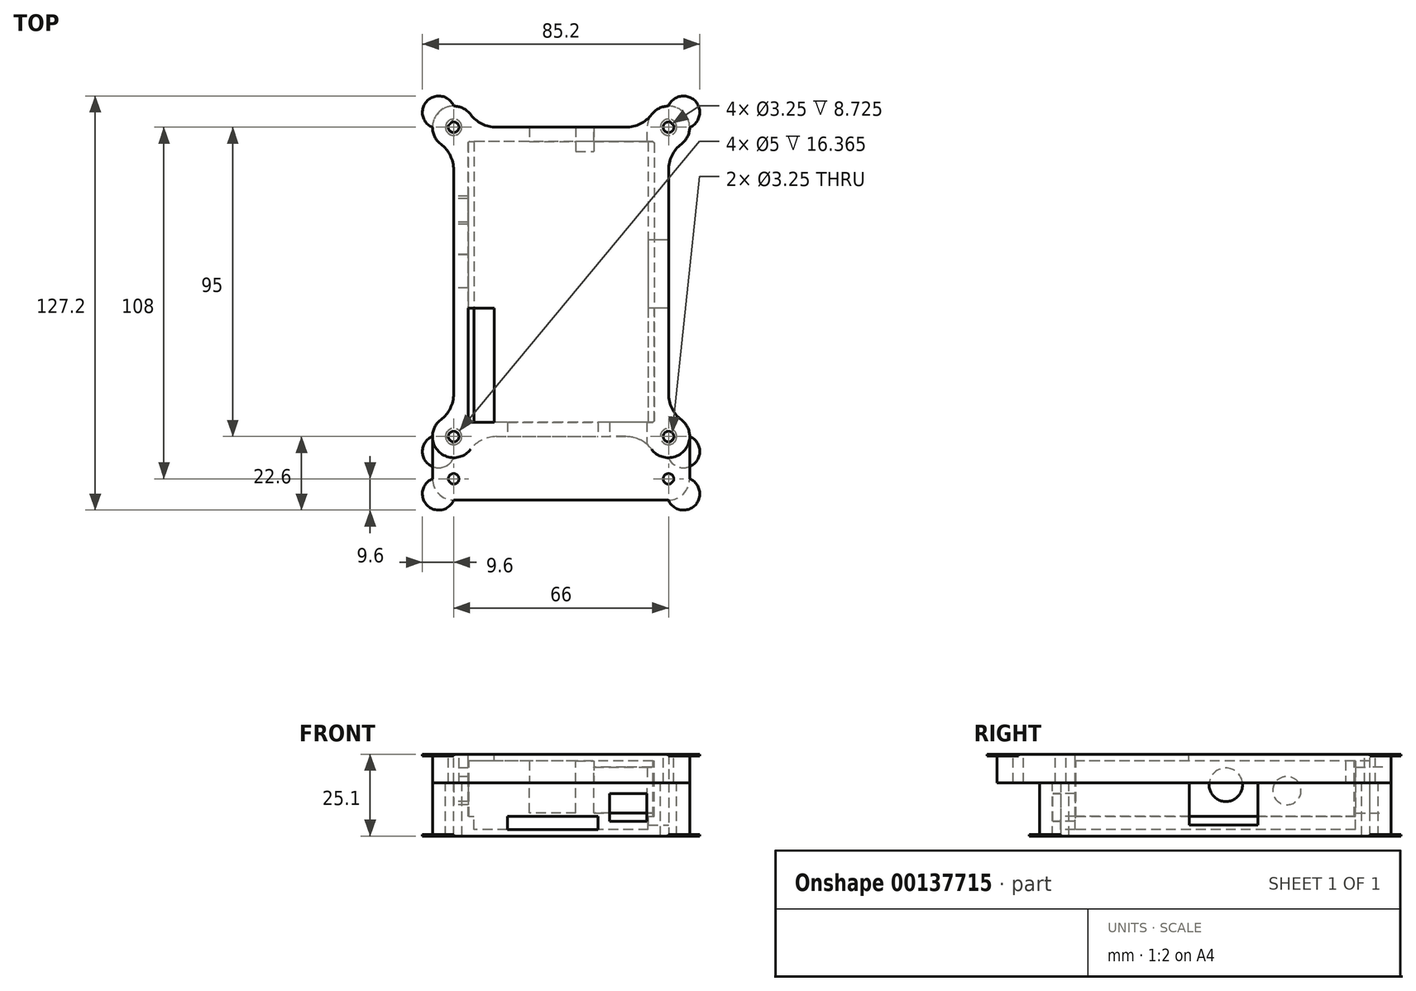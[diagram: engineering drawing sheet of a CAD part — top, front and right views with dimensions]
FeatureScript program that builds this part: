
annotation { "Feature Type Name" : "Feature", "Feature Type Description" : "" }
export const myFeature = defineFeature(function(context is Context, id is Id, definition is map)
    precondition{}
    {
        {
            var Q0;
            Q0=qCreatedBy(makeId("Top.planeOp"),FACE);
            var sketch = newSketch(context, id + "F0", { "sketchPlane" : qUnion([Q0])});
            skLineSegment(sketch, "E0.rect.bottom", {"start": v(28, 42.5) * mm, "end": v(-28, 42.5) * mm, "construction": true});
            skLineSegment(sketch, "E0.rect.top", {"start": v(28, -42.5) * mm, "end": v(-28, -42.5) * mm, "construction": true});
            skLineSegment(sketch, "E0.rect.left", {"start": v(28, 42.5) * mm, "end": v(28, -42.5) * mm, "construction": true});
            skLineSegment(sketch, "E0.rect.right", {"start": v(-28, 42.5) * mm, "end": v(-28, -42.5) * mm, "construction": true});
            skPoint(sketch, "E0.rect.middle", {"position": v(0, 0) * mm});
            skLineSegment(sketch, "E1.0", {"start": v(33, 47.5) * mm, "end": v(-33, 47.5) * mm});
            skLineSegment(sketch, "E1.1", {"start": v(33, 47.5) * mm, "end": v(33, -47.5) * mm});
            skLineSegment(sketch, "E1.2", {"start": v(33, -47.5) * mm, "end": v(-33, -47.5) * mm});
            skLineSegment(sketch, "E1.3", {"start": v(-33, 47.5) * mm, "end": v(-33, -47.5) * mm});
            skSolve(sketch);
        }
        {
            var Q0;
            Q0=qSketchRegion(id+"F0",true);
            extrude(context, id + "F1", {"entities" : qUnion([Q0]), "depth" : (2 + 1.6 + 15.5 + 4) * mm});
        }
        {
            var Q0;
            Q0=makeQuery(id+"F1.opExtrude","CAP_FACE",FACE,{"disambiguationData":[OSD([sQuery(id+"F0.wireOp",EDGE,"E1.0"),sQuery(id+"F0.wireOp",EDGE,"E1.1"),sQuery(id+"F0.wireOp",EDGE,"E1.2"),sQuery(id+"F0.wireOp",EDGE,"E1.3")])],"isStart":false});
            var sketch = newSketch(context, id + "F2", { "sketchPlane" : qUnion([Q0])});
            skLineSegment(sketch, "E2.rect.bottom", {"start": v(28, 42.5) * mm, "end": v(-28, 42.5) * mm});
            skLineSegment(sketch, "E2.rect.top", {"start": v(28, -42.5) * mm, "end": v(-28, -42.5) * mm});
            skLineSegment(sketch, "E2.rect.left", {"start": v(28, 42.5) * mm, "end": v(28, -42.5) * mm});
            skLineSegment(sketch, "E2.rect.right", {"start": v(-28, 42.5) * mm, "end": v(-28, -42.5) * mm});
            skPoint(sketch, "E2.rect.middle", {"position": v(0, 0) * mm});
            skSolve(sketch);
        }
        {
            var Q0;
            Q0=qSketchRegion(id+"F2",true);
            extrude(context, id + "F3", {"entities" : qUnion([Q0]), "operationType" : NewBodyOperationType.REMOVE, "oppositeDirection" : true, "depth" : (15.5 + 1.6) * mm});
        }
        {
            var Q0;
            Q0=makeQuery(id+"F3.boolean.opBoolean","COPY",FACE,{"derivedFrom":makeQuery(id+"F3.opExtrude","CAP_FACE",FACE,{"disambiguationData":[OSD([sQuery(id+"F2.wireOp",EDGE,"E2.rect.bottom"),sQuery(id+"F2.wireOp",EDGE,"E2.rect.top"),sQuery(id+"F2.wireOp",EDGE,"E2.rect.left"),sQuery(id+"F2.wireOp",EDGE,"E2.rect.right")])],"isStart":false})});
            var sketch = newSketch(context, id + "F4", { "sketchPlane" : qUnion([Q0])});
            skLineSegment(sketch, "E3.rect.bottom", {"start": v(26.75, 42.5) * mm, "end": v(-26.75, 42.5) * mm});
            skLineSegment(sketch, "E3.rect.top", {"start": v(26.75, -42.5) * mm, "end": v(-26.75, -42.5) * mm});
            skLineSegment(sketch, "E3.rect.left", {"start": v(26.75, 42.5) * mm, "end": v(26.75, -42.5) * mm});
            skLineSegment(sketch, "E3.rect.right", {"start": v(-26.75, 42.5) * mm, "end": v(-26.75, -42.5) * mm});
            skPoint(sketch, "E3.rect.middle", {"position": v(0, 0) * mm});
            skSolve(sketch);
        }
        {
            var Q0;
            Q0=qSketchRegion(id+"F4",true);
            extrude(context, id + "F5", {"entities" : qUnion([Q0]), "operationType" : NewBodyOperationType.REMOVE, "oppositeDirection" : true, "depth" : 4 * mm});
        }
        {
            var Q0;
            Q0=makeQuery(id+"F1.opExtrude","SWEPT_FACE",FACE,{"disambiguationData":[OSD([sQuery(id+"F0.wireOp",EDGE,"E1.2")])]});
            var sketch = newSketch(context, id + "F6", { "sketchPlane" : qUnion([Q0])});
            skLineSegment(sketch, "E4.0", {"start": v(26.75, 2) * mm, "end": v(-26.75, 2) * mm, "construction": true});
            skLineSegment(sketch, "E4.1", {"start": v(-26.75, 6) * mm, "end": v(-28, 6) * mm, "construction": true});
            skLineSegment(sketch, "E5.bottom", {"start": v(-16.5, 2) * mm, "end": v(11.3, 2) * mm});
            skLineSegment(sketch, "E5.top", {"start": v(-16.5, 6) * mm, "end": v(11.3, 6) * mm});
            skLineSegment(sketch, "E5.left", {"start": v(-16.5, 2) * mm, "end": v(-16.5, 6) * mm});
            skLineSegment(sketch, "E5.right", {"start": v(11.3, 2) * mm, "end": v(11.3, 6) * mm});
            skLineSegment(sketch, "E6.0", {"start": v(28, 6) * mm, "end": v(26.75, 6) * mm, "construction": true});
            skLineSegment(sketch, "E7.bottom", {"start": v(24.4, 7.6) * mm, "end": v(16.8, 7.6) * mm, "construction": true});
            skLineSegment(sketch, "E7.top", {"start": v(24.4, 10) * mm, "end": v(16.8, 10) * mm, "construction": true});
            skLineSegment(sketch, "E7.left", {"start": v(24.4, 7.6) * mm, "end": v(24.4, 10) * mm, "construction": true});
            skLineSegment(sketch, "E7.right", {"start": v(16.8, 7.6) * mm, "end": v(16.8, 10) * mm, "construction": true});
            skLineSegment(sketch, "E8", {"start": v(20.6, 10) * mm, "end": v(20.6, 7.6) * mm, "construction": true});
            skPoint(sketch, "E9", {"position": v(20.6, 8.8) * mm});
            skLineSegment(sketch, "E10.rect.bottom", {"start": v(26.35, 13.05) * mm, "end": v(14.85, 13.05) * mm});
            skLineSegment(sketch, "E10.rect.top", {"start": v(26.35, 4.55) * mm, "end": v(14.85, 4.55) * mm});
            skLineSegment(sketch, "E10.rect.left", {"start": v(26.35, 13.05) * mm, "end": v(26.35, 4.55) * mm});
            skLineSegment(sketch, "E10.rect.right", {"start": v(14.85, 13.05) * mm, "end": v(14.85, 4.55) * mm});
            skSolve(sketch);
        }
        {
            var Q0;
            Q0=qSketchRegion(id+"F6",true);
            var Q1;
            Q1=makeQuery(id+"F5.boolean.opBoolean","MERGE",FACE,{"derivedFrom":[makeQuery(id+"F3.boolean.opBoolean","COPY",FACE,{"derivedFrom":makeQuery(id+"F3.opExtrude","SWEPT_FACE",FACE,{"disambiguationData":[OSD([sQuery(id+"F2.wireOp",EDGE,"E2.rect.top")])]})}),makeQuery(id+"F5.opExtrude","SWEPT_FACE",FACE,{"disambiguationData":[OSD([sQuery(id+"F4.wireOp",EDGE,"E3.rect.top")])]})]});
            extrude(context, id + "F7", {"entities" : qUnion([Q0]), "operationType" : NewBodyOperationType.REMOVE, "endBound" : BoundingType.UP_TO_SURFACE, "oppositeDirection" : true, "endBoundEntityFace" : qUnion([Q1]), "depth" : 25 * mm});
        }
        {
            var Q0;
            Q0=makeQuery(id+"F1.opExtrude","SWEPT_FACE",FACE,{"disambiguationData":[OSD([sQuery(id+"F0.wireOp",EDGE,"E1.0")])]});
            var sketch = newSketch(context, id + "F8", { "sketchPlane" : qUnion([Q0])});
            skLineSegment(sketch, "E11.0", {"start": v(-28, 6) * mm, "end": v(-26.75, 6) * mm, "construction": true});
            skLineSegment(sketch, "E11.1", {"start": v(-26.75, 2) * mm, "end": v(26.75, 2) * mm, "construction": true});
            skLineSegment(sketch, "E11.2", {"start": v(26.75, 6) * mm, "end": v(28, 6) * mm, "construction": true});
            skLineSegment(sketch, "E12.bottom", {"start": v(-26, 7.6) * mm, "end": v(-10.6, 7.6) * mm, "construction": true});
            skLineSegment(sketch, "E12.top", {"start": v(-26, 20.6) * mm, "end": v(-10.6, 20.6) * mm, "construction": true});
            skLineSegment(sketch, "E12.left", {"start": v(-26, 7.6) * mm, "end": v(-26, 20.6) * mm, "construction": true});
            skLineSegment(sketch, "E12.right", {"start": v(-10.6, 7.6) * mm, "end": v(-10.6, 20.6) * mm, "construction": true});
            skLineSegment(sketch, "E13.bottom", {"start": v(-4.05, 7.6) * mm, "end": v(9.2, 7.6) * mm, "construction": true});
            skLineSegment(sketch, "E13.top", {"start": v(-4.05, 23.1) * mm, "end": v(9.2, 23.1) * mm, "construction": true});
            skLineSegment(sketch, "E13.left", {"start": v(-4.05, 7.6) * mm, "end": v(-4.05, 23.1) * mm, "construction": true});
            skLineSegment(sketch, "E13.right", {"start": v(9.2, 7.6) * mm, "end": v(9.2, 23.1) * mm, "construction": true});
            skLineSegment(sketch, "E14.0", {"start": v(-26.5, 21.1) * mm, "end": v(-10.1, 21.1) * mm});
            skLineSegment(sketch, "E14.1", {"start": v(-26.5, 7.1) * mm, "end": v(-26.5, 21.1) * mm});
            skLineSegment(sketch, "E14.2", {"start": v(-26.5, 7.1) * mm, "end": v(-10.1, 7.1) * mm});
            skLineSegment(sketch, "E14.3", {"start": v(-10.1, 7.1) * mm, "end": v(-10.1, 21.1) * mm});
            skLineSegment(sketch, "E15.0", {"start": v(-4.55, 23.6) * mm, "end": v(9.7, 23.6) * mm});
            skLineSegment(sketch, "E15.1", {"start": v(-4.55, 7.1) * mm, "end": v(-4.55, 23.6) * mm});
            skLineSegment(sketch, "E15.2", {"start": v(-4.55, 7.1) * mm, "end": v(9.7, 7.1) * mm});
            skLineSegment(sketch, "E15.3", {"start": v(9.7, 7.1) * mm, "end": v(9.7, 23.6) * mm});
            skSolve(sketch);
        }
        {
            var Q0;
            Q0=qSketchRegion(id+"F8",true);
            var Q1;
            Q1=makeQuery(id+"F5.boolean.opBoolean","MERGE",FACE,{"derivedFrom":[makeQuery(id+"F3.boolean.opBoolean","COPY",FACE,{"derivedFrom":makeQuery(id+"F3.opExtrude","SWEPT_FACE",FACE,{"disambiguationData":[OSD([sQuery(id+"F2.wireOp",EDGE,"E2.rect.bottom")])]})}),makeQuery(id+"F5.opExtrude","SWEPT_FACE",FACE,{"disambiguationData":[OSD([sQuery(id+"F4.wireOp",EDGE,"E3.rect.bottom")])]})]});
            extrude(context, id + "F9", {"entities" : qUnion([Q0]), "operationType" : NewBodyOperationType.REMOVE, "endBound" : BoundingType.UP_TO_SURFACE, "oppositeDirection" : true, "endBoundEntityFace" : qUnion([Q1]), "depth" : 25 * mm});
        }
        {
            var Q0;
            Q0=makeQuery(id+"F1.opExtrude","SWEPT_FACE",FACE,{"disambiguationData":[OSD([sQuery(id+"F0.wireOp",EDGE,"E1.1")])]});
            var sketch = newSketch(context, id + "F10", { "sketchPlane" : qUnion([Q0])});
            skLineSegment(sketch, "E16.0", {"start": v(42.5, 6) * mm, "end": v(-42.5, 6) * mm, "construction": true});
            skLineSegment(sketch, "E17.bottom", {"start": v(-5, 6.8) * mm, "end": v(10.1, 6.8) * mm, "construction": true});
            skLineSegment(sketch, "E17.top", {"start": v(-5, 12.95) * mm, "end": v(10.1, 12.95) * mm, "construction": true});
            skLineSegment(sketch, "E17.left", {"start": v(-5, 6.8) * mm, "end": v(-5, 12.95) * mm, "construction": true});
            skLineSegment(sketch, "E17.right", {"start": v(10.1, 6.8) * mm, "end": v(10.1, 12.95) * mm, "construction": true});
            skLineSegment(sketch, "E18", {"start": v(2.55, 12.95) * mm, "end": v(2.55, 6.8) * mm, "construction": true});
            skPoint(sketch, "E19", {"position": v(2.55, 9.88) * mm});
            skLineSegment(sketch, "E20.rect.bottom", {"start": v(13.05, 16.38) * mm, "end": v(-7.95, 16.38) * mm});
            skLineSegment(sketch, "E20.rect.top", {"start": v(13.05, 3.38) * mm, "end": v(-7.95, 3.38) * mm});
            skLineSegment(sketch, "E20.rect.left", {"start": v(13.05, 16.38) * mm, "end": v(13.05, 3.38) * mm});
            skLineSegment(sketch, "E20.rect.right", {"start": v(-7.95, 16.38) * mm, "end": v(-7.95, 3.38) * mm});
            skSolve(sketch);
        }
        {
            var Q0;
            Q0=qSketchRegion(id+"F10",true);
            var Q1;
            Q1=makeQuery(id+"F5.boolean.opBoolean","COPY",FACE,{"derivedFrom":makeQuery(id+"F5.opExtrude","SWEPT_FACE",FACE,{"disambiguationData":[OSD([sQuery(id+"F4.wireOp",EDGE,"E3.rect.left")])]})});
            extrude(context, id + "F11", {"entities" : qUnion([Q0]), "operationType" : NewBodyOperationType.REMOVE, "endBound" : BoundingType.UP_TO_SURFACE, "oppositeDirection" : true, "endBoundEntityFace" : qUnion([Q1]), "depth" : 25 * mm});
        }
        {
            var Q0;
            Q0=makeQuery(id+"F1.opExtrude","SWEPT_FACE",FACE,{"disambiguationData":[OSD([sQuery(id+"F0.wireOp",EDGE,"E1.3")])]});
            var sketch = newSketch(context, id + "F12", { "sketchPlane" : qUnion([Q0])});
            skLineSegment(sketch, "E21.0", {"start": v(-42.5, 6) * mm, "end": v(42.5, 6) * mm, "construction": true});
            skCircle(sketch, "E22", {"center": v(-22, 13.95) * mm, "radius": 3.35 * mm, "construction": true});
            skCircle(sketch, "E23", {"center": v(-3.25, 15.75) * mm, "radius": 4.15 * mm, "construction": true});
            skPoint(sketch, "E24", {"position": v(-22, 10.6) * mm});
            skPoint(sketch, "E25", {"position": v(-3.25, 11.6) * mm});
            skCircle(sketch, "E26.0", {"center": v(-22, 13.95) * mm, "radius": 4.35 * mm});
            skCircle(sketch, "E27.0", {"center": v(-3.25, 15.75) * mm, "radius": 5.15 * mm});
            skSolve(sketch);
        }
        {
            var Q0;
            Q0=qSketchRegion(id+"F12",true);
            var Q1;
            Q1=makeQuery(id+"F3.boolean.opBoolean","COPY",FACE,{"derivedFrom":makeQuery(id+"F3.opExtrude","SWEPT_FACE",FACE,{"disambiguationData":[OSD([sQuery(id+"F2.wireOp",EDGE,"E2.rect.right")])]})});
            extrude(context, id + "F13", {"entities" : qUnion([Q0]), "operationType" : NewBodyOperationType.REMOVE, "endBound" : BoundingType.UP_TO_SURFACE, "oppositeDirection" : true, "endBoundEntityFace" : qUnion([Q1]), "depth" : 25 * mm});
        }
        {
            var Q0;
            Q0=makeQuery(id+"F1.opExtrude","CAP_FACE",FACE,{"disambiguationData":[OSD([sQuery(id+"F0.wireOp",EDGE,"E1.0"),sQuery(id+"F0.wireOp",EDGE,"E1.1"),sQuery(id+"F0.wireOp",EDGE,"E1.2"),sQuery(id+"F0.wireOp",EDGE,"E1.3")])],"isStart":false});
            var sketch = newSketch(context, id + "F14", { "sketchPlane" : qUnion([Q0])});
            skLineSegment(sketch, "E28.rect.bottom", {"start": v(28.58, 43.08) * mm, "end": v(-28.57, 43.08) * mm});
            skLineSegment(sketch, "E28.rect.top", {"start": v(28.57, -43.07) * mm, "end": v(-28.58, -43.07) * mm});
            skLineSegment(sketch, "E28.rect.left", {"start": v(28.58, 43.08) * mm, "end": v(28.57, -43.07) * mm});
            skLineSegment(sketch, "E28.rect.right", {"start": v(-28.57, 43.08) * mm, "end": v(-28.58, -43.07) * mm});
            skPoint(sketch, "E28.rect.middle", {"position": v(0, 0) * mm});
            skSolve(sketch);
        }
        {
            var Q0;
            Q0=qSketchRegion(id+"F14",true);
            var Q1;
            {var subQ0=sQuery(id+"F2.wireOp",EDGE,"E2.rect.bottom");var subQ1=sQuery(id+"F2.wireOp",EDGE,"E2.rect.top");var subQ2=sQuery(id+"F2.wireOp",EDGE,"E2.rect.right");Q1=makeQuery(id+"F5.boolean.opBoolean","SPLIT",FACE,{"disambiguationData":[TD([makeQuery(id+"F3.boolean.opBoolean","COPY",FACE,{"derivedFrom":makeQuery(id+"F3.opExtrude","SWEPT_FACE",FACE,{"disambiguationData":[OSD([subQ2])]})})])],"derivedFrom":makeQuery(id+"F3.boolean.opBoolean","COPY",FACE,{"derivedFrom":makeQuery(id+"F3.opExtrude","CAP_FACE",FACE,{"disambiguationData":[OSD([subQ0,subQ1,sQuery(id+"F2.wireOp",EDGE,"E2.rect.left"),subQ2])],"isStart":false})})});}
            extrude(context, id + "F15", {"entities" : qUnion([Q0]), "operationType" : NewBodyOperationType.REMOVE, "endBound" : BoundingType.UP_TO_SURFACE, "oppositeDirection" : true, "endBoundEntityFace" : qUnion([Q1]), "depth" : 25 * mm});
        }
        {
            var Q0;
            {var subQ2=sQuery(id+"F2.wireOp",EDGE,"E2.rect.left");var subQ3=makeQuery(id+"F3.boolean.opBoolean","COPY",FACE,{"derivedFrom":makeQuery(id+"F3.opExtrude","SWEPT_FACE",FACE,{"disambiguationData":[OSD([subQ2])]})});var subQ4=sQuery(id+"F2.wireOp",EDGE,"E2.rect.bottom");var subQ5=makeQuery(id+"F3.boolean.opBoolean","COPY",FACE,{"derivedFrom":makeQuery(id+"F3.opExtrude","SWEPT_FACE",FACE,{"disambiguationData":[OSD([subQ4])]})});var subQ6=sQuery(id+"F2.wireOp",EDGE,"E2.rect.top");var subQ9=sQuery(id+"F2.wireOp",EDGE,"E2.rect.right");var subQ10=makeQuery(id+"F3.boolean.opBoolean","COPY",FACE,{"derivedFrom":makeQuery(id+"F3.opExtrude","CAP_FACE",FACE,{"disambiguationData":[OSD([subQ4,subQ6,subQ2,subQ9])],"isStart":false})});Q0=makeQuery(id+"F15.boolean.opBoolean","MERGE",FACE,{"derivedFrom":[makeQuery(id+"F5.boolean.opBoolean","SPLIT",FACE,{"disambiguationData":[TD([makeQuery(id+"F3.boolean.opBoolean","COPY",FACE,{"derivedFrom":makeQuery(id+"F3.opExtrude","SWEPT_FACE",FACE,{"disambiguationData":[OSD([subQ9])]})})])],"derivedFrom":subQ10}),makeQuery(id+"F11.boolean.opBoolean","SPLIT",FACE,{"disambiguationData":[TD([subQ5])],"derivedFrom":makeQuery(id+"F5.boolean.opBoolean","SPLIT",FACE,{"disambiguationData":[TD([subQ3])],"derivedFrom":subQ10})}),makeQuery(id+"F15.opExtrude","CAP_FACE",FACE,{"disambiguationData":[OSD([sQuery(id+"F14.wireOp",EDGE,"E28.rect.bottom"),sQuery(id+"F14.wireOp",EDGE,"E28.rect.top"),sQuery(id+"F14.wireOp",EDGE,"E28.rect.left"),sQuery(id+"F14.wireOp",EDGE,"E28.rect.right")])],"isStart":false})]});}
            var sketch = newSketch(context, id + "F16", { "sketchPlane" : qUnion([Q0])});
            skLineSegment(sketch, "E29.bottom", {"start": v(-26.75, 42.5) * mm, "end": v(26.75, 42.5) * mm});
            skLineSegment(sketch, "E29.top", {"start": v(-26.75, 43.08) * mm, "end": v(26.75, 43.08) * mm});
            skLineSegment(sketch, "E29.left", {"start": v(-26.75, 42.5) * mm, "end": v(-26.75, 43.08) * mm});
            skLineSegment(sketch, "E29.right", {"start": v(26.75, 42.5) * mm, "end": v(26.75, 43.08) * mm});
            skLineSegment(sketch, "E30.bottom", {"start": v(-26.75, -42.5) * mm, "end": v(26.75, -42.5) * mm});
            skLineSegment(sketch, "E30.top", {"start": v(-26.75, -43.07) * mm, "end": v(26.75, -43.07) * mm});
            skLineSegment(sketch, "E30.left", {"start": v(-26.75, -42.5) * mm, "end": v(-26.75, -43.07) * mm});
            skLineSegment(sketch, "E30.right", {"start": v(26.75, -42.5) * mm, "end": v(26.75, -43.07) * mm});
            skSolve(sketch);
        }
        {
            var Q0;
            Q0=qSketchRegion(id+"F16",true);
            var Q1;
            Q1=makeQuery(id+"F7.boolean.opBoolean","MERGE",FACE,{"derivedFrom":[makeQuery(id+"F5.boolean.opBoolean","COPY",FACE,{"derivedFrom":makeQuery(id+"F5.opExtrude","CAP_FACE",FACE,{"disambiguationData":[OSD([sQuery(id+"F4.wireOp",EDGE,"E3.rect.bottom"),sQuery(id+"F4.wireOp",EDGE,"E3.rect.top"),sQuery(id+"F4.wireOp",EDGE,"E3.rect.left"),sQuery(id+"F4.wireOp",EDGE,"E3.rect.right")])],"isStart":false})}),makeQuery(id+"F7.opExtrude","SWEPT_FACE",FACE,{"disambiguationData":[OSD([sQuery(id+"F6.wireOp",EDGE,"E5.bottom")])]})]});
            extrude(context, id + "F17", {"entities" : qUnion([Q0]), "operationType" : NewBodyOperationType.REMOVE, "endBound" : BoundingType.UP_TO_SURFACE, "oppositeDirection" : true, "endBoundEntityFace" : qUnion([Q1]), "depth" : 25 * mm});
        }
        {
            var Q0;
            Q0=makeQuery(id+"F1.opExtrude","CAP_FACE",FACE,{"disambiguationData":[OSD([sQuery(id+"F0.wireOp",EDGE,"E1.0"),sQuery(id+"F0.wireOp",EDGE,"E1.1"),sQuery(id+"F0.wireOp",EDGE,"E1.2"),sQuery(id+"F0.wireOp",EDGE,"E1.3")])],"isStart":false});
            var sketch = newSketch(context, id + "F18", { "sketchPlane" : qUnion([Q0])});
            skLineSegment(sketch, "E31.bottom", {"start": v(-33, 47.5) * mm, "end": v(33, 47.5) * mm});
            skLineSegment(sketch, "E31.top", {"start": v(-33, -47.5) * mm, "end": v(33, -47.5) * mm});
            skLineSegment(sketch, "E31.left", {"start": v(-33, 47.5) * mm, "end": v(-33, -47.5) * mm});
            skLineSegment(sketch, "E31.right", {"start": v(33, 47.5) * mm, "end": v(33, -47.5) * mm});
            skSolve(sketch);
        }
        {
            var Q0;
            Q0=qSketchRegion(id+"F18",true);
            extrude(context, id + "F19", {"entities" : qUnion([Q0]), "operationType" : NewBodyOperationType.ADD, "depth" : 2 * mm});
        }
        {
            var Q0;
            Q0=makeQuery(id+"F19.opExtrude","CAP_FACE",FACE,{"disambiguationData":[OSD([sQuery(id+"F18.wireOp",EDGE,"E31.bottom"),sQuery(id+"F18.wireOp",EDGE,"E31.top"),sQuery(id+"F18.wireOp",EDGE,"E31.left"),sQuery(id+"F18.wireOp",EDGE,"E31.right")])],"isStart":false});
            var sketch = newSketch(context, id + "F20", { "sketchPlane" : qUnion([Q0])});
            skCircle(sketch, "E32", {"center": v(-33, 47.5) * mm, "radius": 6.5 * mm});
            skCircle(sketch, "E33", {"center": v(33, 47.5) * mm, "radius": 6.5 * mm});
            skCircle(sketch, "E34", {"center": v(33, -47.5) * mm, "radius": 6.5 * mm});
            skCircle(sketch, "E35", {"center": v(-33, -47.5) * mm, "radius": 6.5 * mm});
            skSolve(sketch);
        }
        {
            var Q0;
            Q0=qSketchRegion(id+"F20",true);
            var Q1;
            Q1=makeQuery(id+"F1.opExtrude","CAP_FACE",FACE,{"disambiguationData":[OSD([sQuery(id+"F0.wireOp",EDGE,"E1.0"),sQuery(id+"F0.wireOp",EDGE,"E1.1"),sQuery(id+"F0.wireOp",EDGE,"E1.2"),sQuery(id+"F0.wireOp",EDGE,"E1.3")])],"isStart":true});
            extrude(context, id + "F21", {"entities" : qUnion([Q0]), "operationType" : NewBodyOperationType.ADD, "endBound" : BoundingType.UP_TO_SURFACE, "oppositeDirection" : true, "endBoundEntityFace" : qUnion([Q1]), "depth" : 25 * mm});
        }
        {
            var Q0;
            Q0=makeQuery(id+"F21.boolean.opBoolean","MERGE",FACE,{"derivedFrom":[makeQuery(id+"F19.opExtrude","CAP_FACE",FACE,{"disambiguationData":[OSD([sQuery(id+"F18.wireOp",EDGE,"E31.bottom"),sQuery(id+"F18.wireOp",EDGE,"E31.top"),sQuery(id+"F18.wireOp",EDGE,"E31.left"),sQuery(id+"F18.wireOp",EDGE,"E31.right")])],"isStart":false}),makeQuery(id+"F21.opExtrude","CAP_FACE",FACE,{"disambiguationData":[OSD([sQuery(id+"F20.wireOp",EDGE,"E32")])],"isStart":true}),makeQuery(id+"F21.opExtrude","CAP_FACE",FACE,{"disambiguationData":[OSD([sQuery(id+"F20.wireOp",EDGE,"E33")])],"isStart":true}),makeQuery(id+"F21.opExtrude","CAP_FACE",FACE,{"disambiguationData":[OSD([sQuery(id+"F20.wireOp",EDGE,"E34")])],"isStart":true}),makeQuery(id+"F21.opExtrude","CAP_FACE",FACE,{"disambiguationData":[OSD([sQuery(id+"F20.wireOp",EDGE,"E35")])],"isStart":true})]});
            var sketch = newSketch(context, id + "F22", { "sketchPlane" : qUnion([Q0])});
            skCircle(sketch, "E36", {"center": v(-33, -47.5) * mm, "radius": 1.63 * mm});
            skCircle(sketch, "E37", {"center": v(33, -47.5) * mm, "radius": 1.63 * mm});
            skCircle(sketch, "E38", {"center": v(33, 47.5) * mm, "radius": 1.63 * mm});
            skCircle(sketch, "E39", {"center": v(-33, 47.5) * mm, "radius": 1.63 * mm});
            skSolve(sketch);
        }
        {
            var Q0;
            Q0=qSketchRegion(id+"F22",true);
            extrude(context, id + "F23", {"entities" : qUnion([Q0]), "operationType" : NewBodyOperationType.REMOVE, "endBound" : BoundingType.THROUGH_ALL, "oppositeDirection" : true, "depth" : 25 * mm});
        }
        {
            var Q0;
            Q0=makeQuery(id+"F21.boolean.opBoolean","INTERSECT",EDGE,{"derivedFrom":[makeQuery(id+"F19.boolean.opBoolean","MERGE",FACE,{"derivedFrom":[makeQuery(id+"F1.opExtrude","SWEPT_FACE",FACE,{"disambiguationData":[OSD([sQuery(id+"F0.wireOp",EDGE,"E1.3")])]}),makeQuery(id+"F19.opExtrude","SWEPT_FACE",FACE,{"disambiguationData":[OSD([sQuery(id+"F18.wireOp",EDGE,"E31.left")])]})]}),makeQuery(id+"F21.opExtrude","SWEPT_FACE",FACE,{"disambiguationData":[OSD([sQuery(id+"F20.wireOp",EDGE,"E32")])]})]});
            var Q1;
            Q1=makeQuery(id+"F21.boolean.opBoolean","INTERSECT",EDGE,{"derivedFrom":[makeQuery(id+"F19.boolean.opBoolean","MERGE",FACE,{"derivedFrom":[makeQuery(id+"F1.opExtrude","SWEPT_FACE",FACE,{"disambiguationData":[OSD([sQuery(id+"F0.wireOp",EDGE,"E1.3")])]}),makeQuery(id+"F19.opExtrude","SWEPT_FACE",FACE,{"disambiguationData":[OSD([sQuery(id+"F18.wireOp",EDGE,"E31.left")])]})]}),makeQuery(id+"F21.opExtrude","SWEPT_FACE",FACE,{"disambiguationData":[OSD([sQuery(id+"F20.wireOp",EDGE,"E35")])]})]});
            var Q2;
            Q2=makeQuery(id+"F21.boolean.opBoolean","INTERSECT",EDGE,{"derivedFrom":[makeQuery(id+"F19.boolean.opBoolean","MERGE",FACE,{"derivedFrom":[makeQuery(id+"F1.opExtrude","SWEPT_FACE",FACE,{"disambiguationData":[OSD([sQuery(id+"F0.wireOp",EDGE,"E1.2")])]}),makeQuery(id+"F19.opExtrude","SWEPT_FACE",FACE,{"disambiguationData":[OSD([sQuery(id+"F18.wireOp",EDGE,"E31.top")])]})]}),makeQuery(id+"F21.opExtrude","SWEPT_FACE",FACE,{"disambiguationData":[OSD([sQuery(id+"F20.wireOp",EDGE,"E35")])]})]});
            var Q3;
            Q3=makeQuery(id+"F21.boolean.opBoolean","INTERSECT",EDGE,{"derivedFrom":[makeQuery(id+"F19.boolean.opBoolean","MERGE",FACE,{"derivedFrom":[makeQuery(id+"F1.opExtrude","SWEPT_FACE",FACE,{"disambiguationData":[OSD([sQuery(id+"F0.wireOp",EDGE,"E1.2")])]}),makeQuery(id+"F19.opExtrude","SWEPT_FACE",FACE,{"disambiguationData":[OSD([sQuery(id+"F18.wireOp",EDGE,"E31.top")])]})]}),makeQuery(id+"F21.opExtrude","SWEPT_FACE",FACE,{"disambiguationData":[OSD([sQuery(id+"F20.wireOp",EDGE,"E34")])]})]});
            var Q4;
            Q4=makeQuery(id+"F21.boolean.opBoolean","INTERSECT",EDGE,{"derivedFrom":[makeQuery(id+"F19.boolean.opBoolean","MERGE",FACE,{"derivedFrom":[makeQuery(id+"F1.opExtrude","SWEPT_FACE",FACE,{"disambiguationData":[OSD([sQuery(id+"F0.wireOp",EDGE,"E1.1")])]}),makeQuery(id+"F19.opExtrude","SWEPT_FACE",FACE,{"disambiguationData":[OSD([sQuery(id+"F18.wireOp",EDGE,"E31.right")])]})]}),makeQuery(id+"F21.opExtrude","SWEPT_FACE",FACE,{"disambiguationData":[OSD([sQuery(id+"F20.wireOp",EDGE,"E34")])]})]});
            var Q5;
            Q5=makeQuery(id+"F21.boolean.opBoolean","INTERSECT",EDGE,{"derivedFrom":[makeQuery(id+"F19.boolean.opBoolean","MERGE",FACE,{"derivedFrom":[makeQuery(id+"F1.opExtrude","SWEPT_FACE",FACE,{"disambiguationData":[OSD([sQuery(id+"F0.wireOp",EDGE,"E1.1")])]}),makeQuery(id+"F19.opExtrude","SWEPT_FACE",FACE,{"disambiguationData":[OSD([sQuery(id+"F18.wireOp",EDGE,"E31.right")])]})]}),makeQuery(id+"F21.opExtrude","SWEPT_FACE",FACE,{"disambiguationData":[OSD([sQuery(id+"F20.wireOp",EDGE,"E33")])]})]});
            var Q6;
            Q6=makeQuery(id+"F21.boolean.opBoolean","INTERSECT",EDGE,{"derivedFrom":[makeQuery(id+"F19.boolean.opBoolean","MERGE",FACE,{"derivedFrom":[makeQuery(id+"F1.opExtrude","SWEPT_FACE",FACE,{"disambiguationData":[OSD([sQuery(id+"F0.wireOp",EDGE,"E1.0")])]}),makeQuery(id+"F19.opExtrude","SWEPT_FACE",FACE,{"disambiguationData":[OSD([sQuery(id+"F18.wireOp",EDGE,"E31.bottom")])]})]}),makeQuery(id+"F21.opExtrude","SWEPT_FACE",FACE,{"disambiguationData":[OSD([sQuery(id+"F20.wireOp",EDGE,"E33")])]})]});
            var Q7;
            Q7=makeQuery(id+"F21.boolean.opBoolean","INTERSECT",EDGE,{"derivedFrom":[makeQuery(id+"F19.boolean.opBoolean","MERGE",FACE,{"derivedFrom":[makeQuery(id+"F1.opExtrude","SWEPT_FACE",FACE,{"disambiguationData":[OSD([sQuery(id+"F0.wireOp",EDGE,"E1.0")])]}),makeQuery(id+"F19.opExtrude","SWEPT_FACE",FACE,{"disambiguationData":[OSD([sQuery(id+"F18.wireOp",EDGE,"E31.bottom")])]})]}),makeQuery(id+"F21.opExtrude","SWEPT_FACE",FACE,{"disambiguationData":[OSD([sQuery(id+"F20.wireOp",EDGE,"E32")])]})]});
            fillet(context, id + "F24", {"entities" : qUnion([Q0, Q1, Q2, Q3, Q4, Q5, Q6, Q7]), "radius" : 10 * mm, "tangentPropagation" : true, "allowEdgeOverflow" : false});
        }
        {
            var Q0;
            Q0=makeQuery(id+"F19.boolean.opBoolean","MERGE",FACE,{"derivedFrom":[makeQuery(id+"F1.opExtrude","SWEPT_FACE",FACE,{"disambiguationData":[OSD([sQuery(id+"F0.wireOp",EDGE,"E1.1")])]}),makeQuery(id+"F19.opExtrude","SWEPT_FACE",FACE,{"disambiguationData":[OSD([sQuery(id+"F18.wireOp",EDGE,"E31.right")])]})]});
            var sketch = newSketch(context, id + "F25", { "sketchPlane" : qUnion([Q0])});
            skLineSegment(sketch, "E40.bottom", {"start": v(-61.72, 16.38) * mm, "end": v(58.28, 16.38) * mm});
            skLineSegment(sketch, "E40.top", {"start": v(-61.72, 16.37) * mm, "end": v(58.28, 16.37) * mm});
            skLineSegment(sketch, "E40.left", {"start": v(-61.72, 16.38) * mm, "end": v(-61.72, 16.37) * mm});
            skLineSegment(sketch, "E40.right", {"start": v(58.28, 16.38) * mm, "end": v(58.28, 16.37) * mm});
            skSolve(sketch);
        }
        {
            var Q0;
            Q0=qSketchRegion(id+"F25",true);
            extrude(context, id + "F26", {"entities" : qUnion([Q0]), "operationType" : NewBodyOperationType.REMOVE, "endBound" : BoundingType.THROUGH_ALL, "oppositeDirection" : true, "depth" : 25 * mm, "hasSecondDirection" : true, "secondDirectionBound" : SecondDirectionBoundingType.THROUGH_ALL, "secondDirectionOppositeDirection" : false, "secondDirectionDepth" : 25 * mm});
        }
        {
            var Q0;
            Q0=makeQuery(id+"F21.boolean.opBoolean","MERGE",FACE,{"derivedFrom":[makeQuery(id+"F19.opExtrude","CAP_FACE",FACE,{"disambiguationData":[OSD([sQuery(id+"F18.wireOp",EDGE,"E31.bottom"),sQuery(id+"F18.wireOp",EDGE,"E31.top"),sQuery(id+"F18.wireOp",EDGE,"E31.left"),sQuery(id+"F18.wireOp",EDGE,"E31.right")])],"isStart":false}),makeQuery(id+"F21.opExtrude","CAP_FACE",FACE,{"disambiguationData":[OSD([sQuery(id+"F20.wireOp",EDGE,"E32")])],"isStart":true}),makeQuery(id+"F21.opExtrude","CAP_FACE",FACE,{"disambiguationData":[OSD([sQuery(id+"F20.wireOp",EDGE,"E33")])],"isStart":true}),makeQuery(id+"F21.opExtrude","CAP_FACE",FACE,{"disambiguationData":[OSD([sQuery(id+"F20.wireOp",EDGE,"E34")])],"isStart":true}),makeQuery(id+"F21.opExtrude","CAP_FACE",FACE,{"disambiguationData":[OSD([sQuery(id+"F20.wireOp",EDGE,"E35")])],"isStart":true})]});
            var sketch = newSketch(context, id + "F27", { "sketchPlane" : qUnion([Q0])});
            skLineSegment(sketch, "E41.bottom", {"start": v(-28.58, -43.07) * mm, "end": v(-20.57, -43.07) * mm});
            skLineSegment(sketch, "E41.top", {"start": v(-28.58, -8.08) * mm, "end": v(-20.58, -8.08) * mm});
            skLineSegment(sketch, "E41.left", {"start": v(-28.57, -43.07) * mm, "end": v(-28.58, -8.07) * mm});
            skLineSegment(sketch, "E41.right", {"start": v(-20.57, -43.07) * mm, "end": v(-20.58, -8.07) * mm});
            skSolve(sketch);
        }
        {
            var Q0;
            Q0=qSketchRegion(id+"F27",true);
            extrude(context, id + "F28", {"entities" : qUnion([Q0]), "operationType" : NewBodyOperationType.REMOVE, "endBound" : BoundingType.UP_TO_NEXT, "oppositeDirection" : true, "depth" : 3 * mm});
        }
        {
            var Q0;
            {var subQ0=sQuery(id+"F18.wireOp",EDGE,"E31.left");var subQ1=sQuery(id+"F18.wireOp",EDGE,"E31.bottom");var subQ2=sQuery(id+"F0.wireOp",EDGE,"E1.0");var subQ3=sQuery(id+"F0.wireOp",EDGE,"E1.3");var subQ4=sQuery(id+"F20.wireOp",EDGE,"E32");Q0=makeQuery(id+"F26.boolean.opBoolean","COPY",FACE,{"disambiguationData":[TD([makeQuery(id+"F1.opExtrude","SWEPT_FACE",FACE,{"disambiguationData":[OSD([subQ2])]}),makeQuery(id+"F1.opExtrude","SWEPT_FACE",FACE,{"disambiguationData":[OSD([subQ3])]}),makeQuery(id+"F9.boolean.opBoolean","COPY",FACE,{"derivedFrom":makeQuery(id+"F9.opExtrude","SWEPT_FACE",FACE,{"disambiguationData":[OSD([sQuery(id+"F8.wireOp",EDGE,"E15.3")])]})}),makeQuery(id+"F13.boolean.opBoolean","COPY",FACE,{"derivedFrom":makeQuery(id+"F13.opExtrude","SWEPT_FACE",FACE,{"disambiguationData":[OSD([sQuery(id+"F12.wireOp",EDGE,"E26.0")])]})}),makeQuery(id+"F15.boolean.opBoolean","COPY",FACE,{"derivedFrom":makeQuery(id+"F15.opExtrude","SWEPT_FACE",FACE,{"disambiguationData":[OSD([sQuery(id+"F14.wireOp",EDGE,"E28.rect.bottom")])]})}),makeQuery(id+"F15.boolean.opBoolean","COPY",FACE,{"derivedFrom":makeQuery(id+"F15.opExtrude","SWEPT_FACE",FACE,{"disambiguationData":[OSD([sQuery(id+"F14.wireOp",EDGE,"E28.rect.right")])]})}),makeQuery(id+"F17.opExtrude","SWEPT_FACE",FACE,{"disambiguationData":[OSD([sQuery(id+"F16.wireOp",EDGE,"E29.top")])]}),makeQuery(id+"F19.opExtrude","SWEPT_FACE",FACE,{"disambiguationData":[OSD([subQ1])]}),makeQuery(id+"F19.opExtrude","SWEPT_FACE",FACE,{"disambiguationData":[OSD([subQ0])]}),makeQuery(id+"F21.opExtrude","SWEPT_FACE",FACE,{"disambiguationData":[OSD([subQ4])]}),makeQuery(id+"F23.boolean.opBoolean","COPY",FACE,{"derivedFrom":makeQuery(id+"F23.opExtrude","SWEPT_FACE",FACE,{"disambiguationData":[OSD([sQuery(id+"F22.wireOp",EDGE,"E39")])]})}),makeQuery(id+"F24.opFillet","BLEND_FACE",FACE,{"disambiguationData":[OSD([subQ2,subQ1,subQ4])]}),makeQuery(id+"F24.opFillet","BLEND_FACE",FACE,{"disambiguationData":[OSD([subQ3,subQ0,subQ4])]})])],"derivedFrom":makeQuery(id+"F26.opExtrude","SWEPT_FACE",FACE,{"disambiguationData":[OSD([sQuery(id+"F25.wireOp",EDGE,"E40.top")])]})});}
            var sketch = newSketch(context, id + "F29", { "sketchPlane" : qUnion([Q0])});
            skCircle(sketch, "E42", {"center": v(-33, 47.5) * mm, "radius": 2.5 * mm});
            skCircle(sketch, "E43", {"center": v(33, 47.5) * mm, "radius": 2.5 * mm});
            skCircle(sketch, "E44", {"center": v(-33, -47.5) * mm, "radius": 2.5 * mm});
            skCircle(sketch, "E45", {"center": v(33, -47.5) * mm, "radius": 2.5 * mm});
            skSolve(sketch);
        }
        {
            var Q0;
            Q0=qSketchRegion(id+"F29",true);
            var Q1;
            Q1=makeQuery(id+"F17.boolean.opBoolean","MERGE",FACE,{"derivedFrom":[makeQuery(id+"F7.boolean.opBoolean","MERGE",FACE,{"derivedFrom":[makeQuery(id+"F5.boolean.opBoolean","COPY",FACE,{"derivedFrom":makeQuery(id+"F5.opExtrude","CAP_FACE",FACE,{"disambiguationData":[OSD([sQuery(id+"F4.wireOp",EDGE,"E3.rect.bottom"),sQuery(id+"F4.wireOp",EDGE,"E3.rect.top"),sQuery(id+"F4.wireOp",EDGE,"E3.rect.left"),sQuery(id+"F4.wireOp",EDGE,"E3.rect.right")])],"isStart":false})}),makeQuery(id+"F7.opExtrude","SWEPT_FACE",FACE,{"disambiguationData":[OSD([sQuery(id+"F6.wireOp",EDGE,"E5.bottom")])]})]}),makeQuery(id+"F17.opExtrude","CAP_FACE",FACE,{"disambiguationData":[OSD([sQuery(id+"F16.wireOp",EDGE,"E29.bottom"),sQuery(id+"F16.wireOp",EDGE,"E29.top"),sQuery(id+"F16.wireOp",EDGE,"E29.left"),sQuery(id+"F16.wireOp",EDGE,"E29.right")])],"isStart":false}),makeQuery(id+"F17.opExtrude","CAP_FACE",FACE,{"disambiguationData":[OSD([sQuery(id+"F16.wireOp",EDGE,"E30.bottom"),sQuery(id+"F16.wireOp",EDGE,"E30.top"),sQuery(id+"F16.wireOp",EDGE,"E30.left"),sQuery(id+"F16.wireOp",EDGE,"E30.right")])],"isStart":false})]});
            extrude(context, id + "F30", {"entities" : qUnion([Q0]), "operationType" : NewBodyOperationType.REMOVE, "endBound" : BoundingType.UP_TO_SURFACE, "oppositeDirection" : true, "endBoundEntityFace" : qUnion([Q1]), "depth" : 13 * mm});
        }
        {
            var Q0;
            Q0=makeQuery(id+"F21.boolean.opBoolean","MERGE",FACE,{"derivedFrom":[makeQuery(id+"F1.opExtrude","CAP_FACE",FACE,{"disambiguationData":[OSD([sQuery(id+"F0.wireOp",EDGE,"E1.0"),sQuery(id+"F0.wireOp",EDGE,"E1.1"),sQuery(id+"F0.wireOp",EDGE,"E1.2"),sQuery(id+"F0.wireOp",EDGE,"E1.3")])],"isStart":true}),makeQuery(id+"F21.opExtrude","CAP_FACE",FACE,{"disambiguationData":[OSD([sQuery(id+"F20.wireOp",EDGE,"E32")])],"isStart":false}),makeQuery(id+"F21.opExtrude","CAP_FACE",FACE,{"disambiguationData":[OSD([sQuery(id+"F20.wireOp",EDGE,"E33")])],"isStart":false}),makeQuery(id+"F21.opExtrude","CAP_FACE",FACE,{"disambiguationData":[OSD([sQuery(id+"F20.wireOp",EDGE,"E34")])],"isStart":false}),makeQuery(id+"F21.opExtrude","CAP_FACE",FACE,{"disambiguationData":[OSD([sQuery(id+"F20.wireOp",EDGE,"E35")])],"isStart":false})]});
            var sketch = newSketch(context, id + "F31", { "sketchPlane" : qUnion([Q0])});
            skCircle(sketch, "E46.0", {"center": v(-33, -47.5) * mm, "radius": 1.63 * mm});
            skCircle(sketch, "E46.1", {"center": v(-33, 47.5) * mm, "radius": 1.63 * mm});
            skCircle(sketch, "E46.2", {"center": v(33, 47.5) * mm, "radius": 1.63 * mm});
            skCircle(sketch, "E46.3", {"center": v(33, -47.5) * mm, "radius": 1.63 * mm});
            skSolve(sketch);
        }
        {
            var Q0;
            Q0=qSketchRegion(id+"F31",true);
            var Q1;
            Q1=makeQuery(id+"F30.boolean.opBoolean","COPY",FACE,{"derivedFrom":makeQuery(id+"F30.opExtrude","CAP_FACE",FACE,{"disambiguationData":[OSD([sQuery(id+"F29.wireOp",EDGE,"E43")])],"isStart":false})});
            extrude(context, id + "F32", {"entities" : qUnion([Q0]), "operationType" : NewBodyOperationType.ADD, "endBound" : BoundingType.UP_TO_SURFACE, "oppositeDirection" : true, "endBoundEntityFace" : qUnion([Q1]), "depth" : 25 * mm});
        }
        {
            var Q0;
            Q0=makeQuery(id+"F26.boolean.opBoolean","COPY",FACE,{"disambiguationData":[TD([makeQuery(id+"F9.boolean.opBoolean","COPY",FACE,{"derivedFrom":makeQuery(id+"F9.opExtrude","SWEPT_FACE",FACE,{"disambiguationData":[OSD([sQuery(id+"F8.wireOp",EDGE,"E14.3")])]})})])],"derivedFrom":makeQuery(id+"F26.opExtrude","SWEPT_FACE",FACE,{"disambiguationData":[OSD([sQuery(id+"F25.wireOp",EDGE,"E40.bottom")])]})});
            var sketch = newSketch(context, id + "F33", { "sketchPlane" : qUnion([Q0])});
            skLineSegment(sketch, "E47.bottom", {"start": v(4.55, -43.08) * mm, "end": v(10.1, -43.08) * mm});
            skLineSegment(sketch, "E47.top", {"start": v(4.55, -40.08) * mm, "end": v(10.1, -40.08) * mm});
            skLineSegment(sketch, "E47.left", {"start": v(4.55, -43.08) * mm, "end": v(4.55, -40.08) * mm});
            skLineSegment(sketch, "E47.right", {"start": v(10.1, -43.07) * mm, "end": v(10.1, -40.08) * mm});
            skSolve(sketch);
        }
        {
            var Q0;
            Q0=qSketchRegion(id+"F33",true);
            var Q1;
            Q1=makeQuery(id+"F19.opExtrude","CAP_FACE",FACE,{"disambiguationData":[OSD([sQuery(id+"F18.wireOp",EDGE,"E31.bottom"),sQuery(id+"F18.wireOp",EDGE,"E31.top"),sQuery(id+"F18.wireOp",EDGE,"E31.left"),sQuery(id+"F18.wireOp",EDGE,"E31.right")])],"isStart":true});
            extrude(context, id + "F34", {"entities" : qUnion([Q0]), "operationType" : NewBodyOperationType.ADD, "endBound" : BoundingType.UP_TO_SURFACE, "oppositeDirection" : true, "endBoundEntityFace" : qUnion([Q1]), "depth" : 25 * mm});
        }
        {
            var Q0;
            Q0=makeQuery(id+"F32.boolean.opBoolean","MERGE",FACE,{"derivedFrom":[makeQuery(id+"F21.boolean.opBoolean","MERGE",FACE,{"derivedFrom":[makeQuery(id+"F1.opExtrude","CAP_FACE",FACE,{"disambiguationData":[OSD([sQuery(id+"F0.wireOp",EDGE,"E1.0"),sQuery(id+"F0.wireOp",EDGE,"E1.1"),sQuery(id+"F0.wireOp",EDGE,"E1.2"),sQuery(id+"F0.wireOp",EDGE,"E1.3")])],"isStart":true}),makeQuery(id+"F21.opExtrude","CAP_FACE",FACE,{"disambiguationData":[OSD([sQuery(id+"F20.wireOp",EDGE,"E32")])],"isStart":false}),makeQuery(id+"F21.opExtrude","CAP_FACE",FACE,{"disambiguationData":[OSD([sQuery(id+"F20.wireOp",EDGE,"E33")])],"isStart":false}),makeQuery(id+"F21.opExtrude","CAP_FACE",FACE,{"disambiguationData":[OSD([sQuery(id+"F20.wireOp",EDGE,"E34")])],"isStart":false}),makeQuery(id+"F21.opExtrude","CAP_FACE",FACE,{"disambiguationData":[OSD([sQuery(id+"F20.wireOp",EDGE,"E35")])],"isStart":false})]}),makeQuery(id+"F32.opExtrude","CAP_FACE",FACE,{"disambiguationData":[OSD([sQuery(id+"F31.wireOp",EDGE,"E46.0")])],"isStart":true}),makeQuery(id+"F32.opExtrude","CAP_FACE",FACE,{"disambiguationData":[OSD([sQuery(id+"F31.wireOp",EDGE,"E46.1")])],"isStart":true}),makeQuery(id+"F32.opExtrude","CAP_FACE",FACE,{"disambiguationData":[OSD([sQuery(id+"F31.wireOp",EDGE,"E46.2")])],"isStart":true}),makeQuery(id+"F32.opExtrude","CAP_FACE",FACE,{"disambiguationData":[OSD([sQuery(id+"F31.wireOp",EDGE,"E46.3")])],"isStart":true})]});
            var sketch = newSketch(context, id + "F35", { "sketchPlane" : qUnion([Q0])});
            skCircle(sketch, "E48.0", {"center": v(33, 47.5) * mm, "radius": 2.5 * mm});
            skCircle(sketch, "E48.1", {"center": v(-33, 47.5) * mm, "radius": 2.5 * mm});
            skCircle(sketch, "E49.0", {"center": v(33, -47.5) * mm, "radius": 2.5 * mm});
            skCircle(sketch, "E49.1", {"center": v(-33, -47.5) * mm, "radius": 2.5 * mm});
            skSolve(sketch);
        }
        {
            var Q0;
            Q0=qSketchRegion(id+"F35",true);
            var Q1;
            {var subQ0=sQuery(id+"F18.wireOp",EDGE,"E31.left");var subQ1=sQuery(id+"F20.wireOp",EDGE,"E34");var subQ2=sQuery(id+"F18.wireOp",EDGE,"E31.top");var subQ3=sQuery(id+"F0.wireOp",EDGE,"E1.2");var subQ4=sQuery(id+"F18.wireOp",EDGE,"E31.right");var subQ5=sQuery(id+"F20.wireOp",EDGE,"E35");var subQ6=sQuery(id+"F0.wireOp",EDGE,"E1.1");var subQ7=sQuery(id+"F0.wireOp",EDGE,"E1.3");Q1=makeQuery(id+"F26.boolean.opBoolean","COPY",FACE,{"disambiguationData":[TD([makeQuery(id+"F1.opExtrude","SWEPT_FACE",FACE,{"disambiguationData":[OSD([subQ6])]}),makeQuery(id+"F1.opExtrude","SWEPT_FACE",FACE,{"disambiguationData":[OSD([subQ3])]}),makeQuery(id+"F1.opExtrude","SWEPT_FACE",FACE,{"disambiguationData":[OSD([subQ7])]}),makeQuery(id+"F11.boolean.opBoolean","COPY",FACE,{"derivedFrom":makeQuery(id+"F11.opExtrude","SWEPT_FACE",FACE,{"disambiguationData":[OSD([sQuery(id+"F10.wireOp",EDGE,"E20.rect.right")])]})}),makeQuery(id+"F13.boolean.opBoolean","COPY",FACE,{"derivedFrom":makeQuery(id+"F13.opExtrude","SWEPT_FACE",FACE,{"disambiguationData":[OSD([sQuery(id+"F12.wireOp",EDGE,"E27.0")])]})}),makeQuery(id+"F15.boolean.opBoolean","COPY",FACE,{"derivedFrom":makeQuery(id+"F15.opExtrude","SWEPT_FACE",FACE,{"disambiguationData":[OSD([sQuery(id+"F14.wireOp",EDGE,"E28.rect.top")])]})}),makeQuery(id+"F15.boolean.opBoolean","COPY",FACE,{"derivedFrom":makeQuery(id+"F15.opExtrude","SWEPT_FACE",FACE,{"disambiguationData":[OSD([sQuery(id+"F14.wireOp",EDGE,"E28.rect.left")])]})}),makeQuery(id+"F15.boolean.opBoolean","COPY",FACE,{"derivedFrom":makeQuery(id+"F15.opExtrude","SWEPT_FACE",FACE,{"disambiguationData":[OSD([sQuery(id+"F14.wireOp",EDGE,"E28.rect.right")])]})}),makeQuery(id+"F17.opExtrude","SWEPT_FACE",FACE,{"disambiguationData":[OSD([sQuery(id+"F16.wireOp",EDGE,"E30.top")])]}),makeQuery(id+"F19.opExtrude","SWEPT_FACE",FACE,{"disambiguationData":[OSD([subQ2])]}),makeQuery(id+"F19.opExtrude","SWEPT_FACE",FACE,{"disambiguationData":[OSD([subQ0])]}),makeQuery(id+"F19.opExtrude","SWEPT_FACE",FACE,{"disambiguationData":[OSD([subQ4])]}),makeQuery(id+"F21.opExtrude","SWEPT_FACE",FACE,{"disambiguationData":[OSD([subQ1])]}),makeQuery(id+"F21.opExtrude","SWEPT_FACE",FACE,{"disambiguationData":[OSD([subQ5])]}),makeQuery(id+"F23.boolean.opBoolean","COPY",FACE,{"derivedFrom":makeQuery(id+"F23.opExtrude","SWEPT_FACE",FACE,{"disambiguationData":[OSD([sQuery(id+"F22.wireOp",EDGE,"E36")])]})}),makeQuery(id+"F23.boolean.opBoolean","COPY",FACE,{"derivedFrom":makeQuery(id+"F23.opExtrude","SWEPT_FACE",FACE,{"disambiguationData":[OSD([sQuery(id+"F22.wireOp",EDGE,"E37")])]})}),makeQuery(id+"F24.opFillet","BLEND_FACE",FACE,{"disambiguationData":[OSD([subQ3,subQ2,subQ1])]}),makeQuery(id+"F24.opFillet","BLEND_FACE",FACE,{"disambiguationData":[OSD([subQ3,subQ2,subQ5])]}),makeQuery(id+"F24.opFillet","BLEND_FACE",FACE,{"disambiguationData":[OSD([subQ6,subQ4,subQ1])]}),makeQuery(id+"F24.opFillet","BLEND_FACE",FACE,{"disambiguationData":[OSD([subQ7,subQ0,subQ5])]})])],"derivedFrom":makeQuery(id+"F26.opExtrude","SWEPT_FACE",FACE,{"disambiguationData":[OSD([sQuery(id+"F25.wireOp",EDGE,"E40.top")])]})});}
            extrude(context, id + "F36", {"entities" : qUnion([Q0]), "operationType" : NewBodyOperationType.REMOVE, "endBound" : BoundingType.UP_TO_SURFACE, "oppositeDirection" : true, "endBoundEntityFace" : qUnion([Q1]), "depth" : 25 * mm});
        }
        {
            var Q0;
            Q0=makeQuery(id+"F32.boolean.opBoolean","MERGE",FACE,{"derivedFrom":[makeQuery(id+"F21.boolean.opBoolean","MERGE",FACE,{"derivedFrom":[makeQuery(id+"F1.opExtrude","CAP_FACE",FACE,{"disambiguationData":[OSD([sQuery(id+"F0.wireOp",EDGE,"E1.0"),sQuery(id+"F0.wireOp",EDGE,"E1.1"),sQuery(id+"F0.wireOp",EDGE,"E1.2"),sQuery(id+"F0.wireOp",EDGE,"E1.3")])],"isStart":true}),makeQuery(id+"F21.opExtrude","CAP_FACE",FACE,{"disambiguationData":[OSD([sQuery(id+"F20.wireOp",EDGE,"E32")])],"isStart":false}),makeQuery(id+"F21.opExtrude","CAP_FACE",FACE,{"disambiguationData":[OSD([sQuery(id+"F20.wireOp",EDGE,"E33")])],"isStart":false}),makeQuery(id+"F21.opExtrude","CAP_FACE",FACE,{"disambiguationData":[OSD([sQuery(id+"F20.wireOp",EDGE,"E34")])],"isStart":false}),makeQuery(id+"F21.opExtrude","CAP_FACE",FACE,{"disambiguationData":[OSD([sQuery(id+"F20.wireOp",EDGE,"E35")])],"isStart":false})]}),makeQuery(id+"F32.opExtrude","CAP_FACE",FACE,{"disambiguationData":[OSD([sQuery(id+"F31.wireOp",EDGE,"E46.0")])],"isStart":true}),makeQuery(id+"F32.opExtrude","CAP_FACE",FACE,{"disambiguationData":[OSD([sQuery(id+"F31.wireOp",EDGE,"E46.1")])],"isStart":true}),makeQuery(id+"F32.opExtrude","CAP_FACE",FACE,{"disambiguationData":[OSD([sQuery(id+"F31.wireOp",EDGE,"E46.2")])],"isStart":true}),makeQuery(id+"F32.opExtrude","CAP_FACE",FACE,{"disambiguationData":[OSD([sQuery(id+"F31.wireOp",EDGE,"E46.3")])],"isStart":true})]});
            var sketch = newSketch(context, id + "F37", { "sketchPlane" : qUnion([Q0])});
            skCircle(sketch, "E50", {"center": v(37.6, 52.1) * mm, "radius": 5 * mm});
            skCircle(sketch, "E51", {"center": v(37.6, -52.1) * mm, "radius": 5 * mm});
            skCircle(sketch, "E52", {"center": v(-37.6, -52.1) * mm, "radius": 5 * mm});
            skCircle(sketch, "E53", {"center": v(-37.6, 52.1) * mm, "radius": 5 * mm});
            skSolve(sketch);
        }
        {
            var Q0;
            Q0=qSketchRegion(id+"F37",true);
            extrude(context, id + "F38", {"entities" : qUnion([Q0]), "operationType" : NewBodyOperationType.ADD, "oppositeDirection" : true, "depth" : 0.5 * mm});
        }
        {
            var Q0;
            Q0=makeQuery(id+"F21.boolean.opBoolean","MERGE",FACE,{"derivedFrom":[makeQuery(id+"F19.opExtrude","CAP_FACE",FACE,{"disambiguationData":[OSD([sQuery(id+"F18.wireOp",EDGE,"E31.bottom"),sQuery(id+"F18.wireOp",EDGE,"E31.top"),sQuery(id+"F18.wireOp",EDGE,"E31.left"),sQuery(id+"F18.wireOp",EDGE,"E31.right")])],"isStart":false}),makeQuery(id+"F21.opExtrude","CAP_FACE",FACE,{"disambiguationData":[OSD([sQuery(id+"F20.wireOp",EDGE,"E32")])],"isStart":true}),makeQuery(id+"F21.opExtrude","CAP_FACE",FACE,{"disambiguationData":[OSD([sQuery(id+"F20.wireOp",EDGE,"E33")])],"isStart":true}),makeQuery(id+"F21.opExtrude","CAP_FACE",FACE,{"disambiguationData":[OSD([sQuery(id+"F20.wireOp",EDGE,"E34")])],"isStart":true}),makeQuery(id+"F21.opExtrude","CAP_FACE",FACE,{"disambiguationData":[OSD([sQuery(id+"F20.wireOp",EDGE,"E35")])],"isStart":true})]});
            var sketch = newSketch(context, id + "F39", { "sketchPlane" : qUnion([Q0])});
            skLineSegment(sketch, "E54", {"start": v(0, -47.5) * mm, "end": v(0, 0) * mm, "construction": true});
            skLineSegment(sketch, "E55", {"start": v(-33, -47.5) * mm, "end": v(-33, -60.5) * mm, "construction": true});
            skCircle(sketch, "E56", {"center": v(-33, -60.5) * mm, "radius": 1.63 * mm});
            skArc(sketch, "E57.0", {"start": v(-39.5, -47.5) * mm, "mid": v(-35.08, -53.66) * mm, "end": v(-27.83, -51.44) * mm});
            skArc(sketch, "E57.1", {"start": v(-27.83, -51.44) * mm, "mid": v(-24.31, -48.54) * mm, "end": v(-19.88, -47.5) * mm});
            skArc(sketch, "E58", {"start": v(-39.5, -60.5) * mm, "mid": v(-37.6, -65.1) * mm, "end": v(-33, -67) * mm});
            skLineSegment(sketch, "E59", {"start": v(-39.5, -47.5) * mm, "end": v(-39.5, -60.5) * mm});
            skCircle(sketch, "E60", {"center": v(-33, -60.5) * mm, "radius": 6.5 * mm, "construction": true});
            skPoint(sketch, "E61.orphan", {"position": v(-36.94, -42.33) * mm});
            skLineSegment(sketch, "E62.MirrorCS", {"start": v(39.5, -47.5) * mm, "end": v(39.5, -60.5) * mm});
            skPoint(sketch, "E63.MirrorP", {"position": v(36.94, -42.33) * mm});
            skArc(sketch, "E64.MirrorCS", {"start": v(39.5, -47.5) * mm, "mid": v(35.08, -53.66) * mm, "end": v(27.83, -51.44) * mm});
            skArc(sketch, "E65.MirrorCS", {"start": v(39.5, -60.5) * mm, "mid": v(37.6, -65.1) * mm, "end": v(33, -67) * mm});
            skCircle(sketch, "E66.MirrorC", {"center": v(33, -60.5) * mm, "radius": 1.63 * mm});
            skArc(sketch, "E67.MirrorCS", {"start": v(27.83, -51.44) * mm, "mid": v(24.31, -48.54) * mm, "end": v(19.88, -47.5) * mm});
            skLineSegment(sketch, "E68", {"start": v(-19.88, -47.5) * mm, "end": v(19.88, -47.5) * mm});
            skLineSegment(sketch, "E69", {"start": v(-33, -67) * mm, "end": v(33, -67) * mm});
            skSolve(sketch);
        }
        {
            var Q0;
            Q0=qSketchRegion(id+"F39",true);
            var Q1;
            Q1=makeQuery(id+"F26.boolean.opBoolean","MERGE",FACE,{"derivedFrom":[makeQuery(id+"F11.boolean.opBoolean","COPY",FACE,{"derivedFrom":makeQuery(id+"F11.opExtrude","SWEPT_FACE",FACE,{"disambiguationData":[OSD([sQuery(id+"F10.wireOp",EDGE,"E20.rect.bottom")])]})}),makeQuery(id+"F26.opExtrude","SWEPT_FACE",FACE,{"disambiguationData":[OSD([sQuery(id+"F25.wireOp",EDGE,"E40.bottom")])]})]});
            extrude(context, id + "F40", {"entities" : qUnion([Q0]), "operationType" : NewBodyOperationType.ADD, "endBound" : BoundingType.UP_TO_SURFACE, "oppositeDirection" : true, "endBoundEntityFace" : qUnion([Q1]), "depth" : 25 * mm});
        }
        {
            var Q0;
            Q0=makeQuery(id+"F40.boolean.opBoolean","MERGE",FACE,{"derivedFrom":[makeQuery(id+"F21.boolean.opBoolean","MERGE",FACE,{"derivedFrom":[makeQuery(id+"F19.opExtrude","CAP_FACE",FACE,{"disambiguationData":[OSD([sQuery(id+"F18.wireOp",EDGE,"E31.bottom"),sQuery(id+"F18.wireOp",EDGE,"E31.top"),sQuery(id+"F18.wireOp",EDGE,"E31.left"),sQuery(id+"F18.wireOp",EDGE,"E31.right")])],"isStart":false}),makeQuery(id+"F21.opExtrude","CAP_FACE",FACE,{"disambiguationData":[OSD([sQuery(id+"F20.wireOp",EDGE,"E32")])],"isStart":true}),makeQuery(id+"F21.opExtrude","CAP_FACE",FACE,{"disambiguationData":[OSD([sQuery(id+"F20.wireOp",EDGE,"E33")])],"isStart":true}),makeQuery(id+"F21.opExtrude","CAP_FACE",FACE,{"disambiguationData":[OSD([sQuery(id+"F20.wireOp",EDGE,"E34")])],"isStart":true}),makeQuery(id+"F21.opExtrude","CAP_FACE",FACE,{"disambiguationData":[OSD([sQuery(id+"F20.wireOp",EDGE,"E35")])],"isStart":true})]}),makeQuery(id+"F40.opExtrude","CAP_FACE",FACE,{"disambiguationData":[OSD([sQuery(id+"F39.wireOp",EDGE,"E56"),sQuery(id+"F39.wireOp",EDGE,"E57.0"),sQuery(id+"F39.wireOp",EDGE,"E57.1"),sQuery(id+"F39.wireOp",EDGE,"E58"),sQuery(id+"F39.wireOp",EDGE,"E59"),sQuery(id+"F39.wireOp",EDGE,"E62.MirrorCS"),sQuery(id+"F39.wireOp",EDGE,"E64.MirrorCS"),sQuery(id+"F39.wireOp",EDGE,"E65.MirrorCS"),sQuery(id+"F39.wireOp",EDGE,"E66.MirrorC"),sQuery(id+"F39.wireOp",EDGE,"E67.MirrorCS"),sQuery(id+"F39.wireOp",EDGE,"E68"),sQuery(id+"F39.wireOp",EDGE,"E69")])],"isStart":true})]});
            var sketch = newSketch(context, id + "F41", { "sketchPlane" : qUnion([Q0])});
            skCircle(sketch, "E70", {"center": v(-37.6, -65.1) * mm, "radius": 5 * mm});
            skCircle(sketch, "E71", {"center": v(-37.6, 52.1) * mm, "radius": 5 * mm});
            skCircle(sketch, "E72", {"center": v(37.6, 52.1) * mm, "radius": 5 * mm});
            skCircle(sketch, "E73", {"center": v(37.6, -65.1) * mm, "radius": 5 * mm});
            skSolve(sketch);
        }
        {
            var Q0;
            Q0=qSketchRegion(id+"F41",true);
            extrude(context, id + "F42", {"entities" : qUnion([Q0]), "operationType" : NewBodyOperationType.ADD, "oppositeDirection" : true, "depth" : 0.5 * mm});
        }
    });
